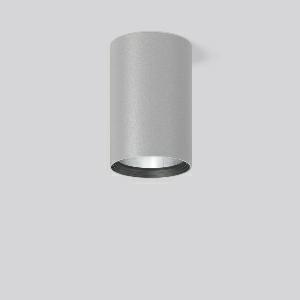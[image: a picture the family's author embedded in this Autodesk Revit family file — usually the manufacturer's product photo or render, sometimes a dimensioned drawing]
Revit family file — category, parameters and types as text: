
# Revit family: heledon_maxi_a_931223_004_2_5b7b
name_source: partatom
category: Lighting Fixtures
units: mm (PartAtom-declared; Revit-internal decimal feet)

## family parameters
Cut with Voids When Loaded = No
Host = Face
Light Source = No
Part Type = Normal
Room Calculation Point = No
Round Connector Dimension = Use Diameter
Shared = No

## types (1)
- HELEDON maxi A (1 x LED Modul 927, 4000 lm, 2700)
    Apparent Load = 35 VA
    Approval mark = CE
    CIE Flux Codes = 100 100 100 100 100
    Color Rendering = 92
    Color Temperature = 2700
    Default Elevation = 1800 mm
    Description = Series: HELEDON maxi
Cylindrical surface-mounted downlight. Housing: die-cast aluminium, powder-coated. Internal ceiling frame polycarbonate with bayonet mounting. Black plastic ring and recessed LED to prevent glare from the side. Optical assembly with reflector made of MIRO-Silver with 98% total light reflection for outstanding efficiency - can be changed without tools. Best colour rendering index Ra>90. Suitable for Ceiling mounting. Easy installation with a separate ceiling frame with bayonet mounting and plug connection. Driver integrated. Connected via plug-in connector. High quality converter without flickering and stroboscopic effect. The following accessories can be mounted without use of tools: interchangeable lenses, decorative glasses, honeycomb louvre, clear and frosted diffusers, white interchangeable plastic ring. 
Colour: silver
Diameter: 123 mm
Height: 183 mm
Lamp: LED
Socket: without socket
Colour temperature: 2700K
Colour rendering index (CRI): 92
System power: 35 W
Rated luminous flux: 4000 lm
Luminous efficiency: 114 lm/W
Control gear: Regulated power supply
Protection class: I
Type of protection: IP 20
    Height = 183 mm
    Lamp = 1 x LED Modul 927
    Lamp Light Flux = 4000 lm
    Lamp count = 1
    Length = 123 mm
    Lifetime = 50000 h
    Luminous efficacy = 114 lm/W
    Manufacturer = RZB
    ModVariant = No
    Model = 931223.004.2
    Mounting Place = Ceiling
    Mounting Type = Surface mounted
    Number of Poles = 1
    OnlyDefault = Yes
    Power Factor = 1
    Product Name = HELEDON maxi A
    Product group = Surface mounted downlights
    ProductGroupID = 302
    Protection Class = Protection class I
    Protection Degree = IP 20
    RLX_Detail_Level = 1
    RLX_Emergency_Light_Flux = 0 lm
    RLX_Emergency_Type = 0
    RLX_Emergency_Type_DB = No
    RlxData = <blob elided: 100037 chars, md5=00512c92>
    Socket = socket
    Standby Power = 0 W
    System Light Flux = 4000 lm
    System Power = 35 W
    Type Comments = Product without accessories
    Type Image = 931192.004.jpg
    URL = http://relux.com
    VarID = ---
    Voltage = 230 V
    Voltage Range = 220-240 V
    Weight = 0.00 kg
    Width = 0 mm  [stored 0 ft]

note: [stored X ft] marks values corroborated as IEEE doubles in the binary element streams (Revit-internal decimal feet)

## geometry (parser evidence)
native form markers: Blend x4, Sweep x12
no freeform markers — native parametric forms only
